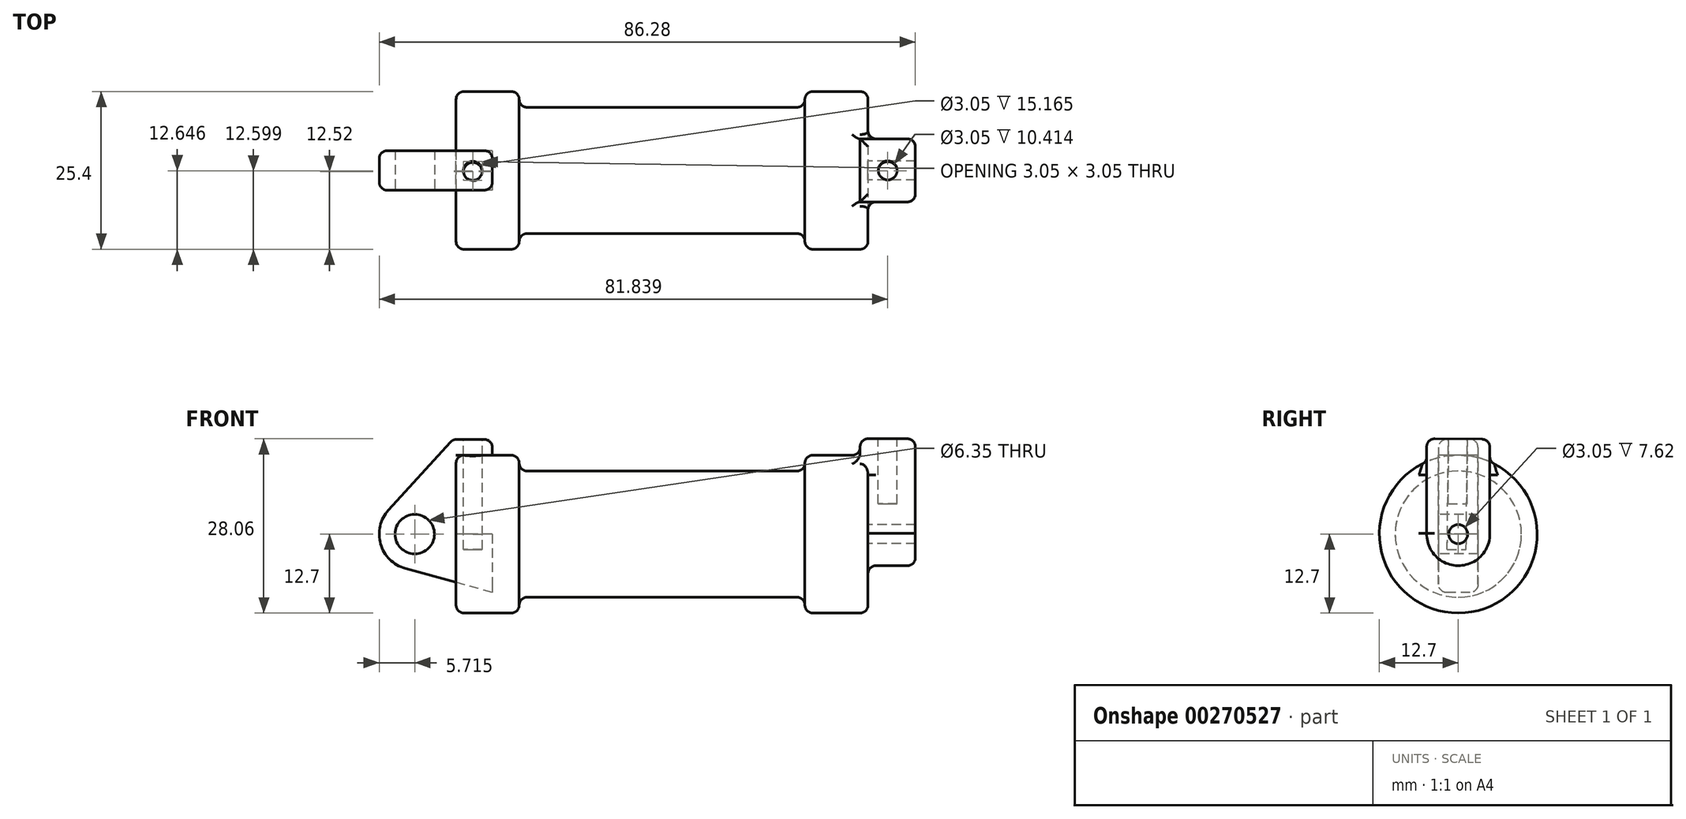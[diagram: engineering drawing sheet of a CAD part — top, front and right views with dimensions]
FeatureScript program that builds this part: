
annotation { "Feature Type Name" : "Feature", "Feature Type Description" : "" }
export const myFeature = defineFeature(function(context is Context, id is Id, definition is map)
    precondition{}
    {
        {
            var Q0;
            Q0=qCreatedBy(makeId("Front.planeOp"),FACE);
            var sketch = newSketch(context, id + "F0", { "sketchPlane" : qUnion([Q0])});
            skLineSegment(sketch, "E0", {"start": v(0, 0) * mm, "end": v(0, 12.7) * mm});
            skLineSegment(sketch, "E1", {"start": v(0, 12.7) * mm, "end": v(10.16, 12.7) * mm});
            skLineSegment(sketch, "E2", {"start": v(10.16, 12.7) * mm, "end": v(10.16, 10.16) * mm});
            skLineSegment(sketch, "E3", {"start": v(10.16, 10.16) * mm, "end": v(56.13, 10.16) * mm});
            skLineSegment(sketch, "E4", {"start": v(56.13, 10.16) * mm, "end": v(56.13, 12.7) * mm});
            skLineSegment(sketch, "E5", {"start": v(56.13, 12.7) * mm, "end": v(66.3, 12.7) * mm});
            skLineSegment(sketch, "E6", {"start": v(66.3, 12.7) * mm, "end": v(66.3, 0) * mm});
            skLineSegment(sketch, "E7", {"start": v(66.3, 0) * mm, "end": v(0, 0) * mm});
            skLineSegment(sketch, "E8", {"start": v(5.84, 15.24) * mm, "end": v(-0.5, 15.24) * mm});
            skLineSegment(sketch, "E9", {"start": v(-0.5, 15.24) * mm, "end": v(-10.88, 3.85) * mm});
            skLineSegment(sketch, "E10", {"start": v(0, 0) * mm, "end": v(-6.65, 0) * mm});
            skCircle(sketch, "E11", {"center": v(-6.65, 0) * mm, "radius": 5.72 * mm});
            skCircle(sketch, "E12", {"center": v(-6.65, 0) * mm, "radius": 3.18 * mm});
            skLineSegment(sketch, "E13", {"start": v(5.84, 15.24) * mm, "end": v(5.84, -9.4) * mm});
            skLineSegment(sketch, "E14", {"start": v(5.84, -9.4) * mm, "end": v(-8.18, -5.5) * mm});
            skSolve(sketch);
        }
        {
            var Q0;
            {var subQ0=sQuery(id+"F0.wireOp",EDGE,"E2");Q0=makeQuery(id+"F0.imprint","IMPRINT",FACE,{"disambiguationData":[TD([[makeQuery(id+"F0.imprint","IMPRINT",EDGE,{"derivedFrom":subQ0}),-1.0]])]});}
            var Q1;
            {var subQ0=sQuery(id+"F0.wireOp",EDGE,"E0");Q1=makeQuery(id+"F0.imprint","IMPRINT",FACE,{"disambiguationData":[TD([[makeQuery(id+"F0.imprint","IMPRINT",EDGE,{"derivedFrom":subQ0}),-1.0]])]});}
            var Q2;
            Q2=sQuery(id+"F0.wireOp",EDGE,"E7");
            revolve(context, id + "F1", {"entities" : qUnion([Q0, Q1]), "axis" : qUnion([Q2]), "revolveType" : RevolveType.FULL});
        }
        {
            var Q0;
            {var subQ3=sQuery(id+"F0.wireOp",EDGE,"E0");Q0=makeQuery(id+"F0.imprint","IMPRINT",FACE,{"disambiguationData":[TD([[makeQuery(id+"F0.imprint","IMPRINT",EDGE,{"derivedFrom":subQ3}),1.0]])]});}
            var Q1;
            {var subQ4=sQuery(id+"F0.wireOp",EDGE,"E12");Q1=makeQuery(id+"F0.imprint","IMPRINT",FACE,{"disambiguationData":[TD([[makeQuery(id+"F0.imprint","IMPRINT",EDGE,{"derivedFrom":subQ4}),-1.0]])]});}
            var Q2;
            {var subQ0=sQuery(id+"F0.wireOp",EDGE,"E14");Q2=makeQuery(id+"F0.imprint","IMPRINT",FACE,{"disambiguationData":[TD([[makeQuery(id+"F0.imprint","IMPRINT",EDGE,{"derivedFrom":subQ0}),-1.0]])]});}
            extrude(context, id + "F2", {"entities" : qUnion([Q0, Q1, Q2]), "endBound" : BoundingType.SYMMETRIC, "oppositeDirection" : true, "depth" : 6.35 * mm});
        }
        {
            var Q0;
            Q0=makeQuery(id+"F1.opRevolve","SWEPT_FACE",FACE,{"disambiguationData":[OSD([sQuery(id+"F0.wireOp",EDGE,"E6")])]});
            var sketch = newSketch(context, id + "F3", { "sketchPlane" : qUnion([Q0])});
            skCircle(sketch, "E15", {"center": v(0, 0) * mm, "radius": 5.08 * mm});
            skCircle(sketch, "E16", {"center": v(0, 0) * mm, "radius": 1.52 * mm});
            skLineSegment(sketch, "E17", {"start": v(5.08, 0.02) * mm, "end": v(5.08, 15.26) * mm});
            skLineSegment(sketch, "E18", {"start": v(-5.08, 0.13) * mm, "end": v(-5.08, 15.37) * mm});
            skLineSegment(sketch, "E19", {"start": v(-5.08, 15.37) * mm, "end": v(5.08, 15.26) * mm});
            skSolve(sketch);
        }
        {
            var Q0;
            Q0 = qSketchRegion(id + "F3", true);
            extrude(context, id + "F4", {"entities" : qUnion([Q0]), "operationType" : NewBodyOperationType.ADD, "depth" : 7.62 * mm, "hasSecondDirection" : true, "secondDirectionOppositeDirection" : true, "secondDirectionDepth" : 1.27 * mm});
        }
        {
            var Q0;
            Q0=makeQuery(id+"F4.opExtrude","SWEPT_FACE",FACE,{"disambiguationData":[OSD([sQuery(id+"F3.wireOp",EDGE,"E19")])]});
            var sketch = newSketch(context, id + "F5", { "sketchPlane" : qUnion([Q0])});
            skCircle(sketch, "E20", {"center": v(69.62, -0.46) * mm, "radius": 1.52 * mm});
            skCircle(sketch, "E21", {"center": v(2.69, -0.23) * mm, "radius": 1.52 * mm});
            skSolve(sketch);
        }
        {
            var Q0;
            Q0=makeQuery(id+"F5.imprint","IMPRINT",FACE,{"disambiguationData":[TD([[makeQuery(id+"F5.imprint","IMPRINT",EDGE,{"derivedFrom":sQuery(id+"F5.wireOp",EDGE,"E21")}),1.0]])]});
            extrude(context, id + "F6", {"entities" : qUnion([Q0]), "operationType" : NewBodyOperationType.REMOVE, "oppositeDirection" : true, "depth" : 17.78 * mm});
        }
        {
            var Q0;
            Q0=makeQuery(id+"F4.opExtrude","SWEPT_FACE",FACE,{"disambiguationData":[OSD([sQuery(id+"F3.wireOp",EDGE,"E19")])]});
            var sketch = newSketch(context, id + "F7", { "sketchPlane" : qUnion([Q0])});
            skCircle(sketch, "E22", {"center": v(69.47, -0.16) * mm, "radius": 1.52 * mm});
            skPoint(sketch, "E22.centerSnap0", {"position": v(69.47, -5.24) * mm});
            skPoint(sketch, "E22.centerSnap1", {"position": v(73.91, -0.16) * mm});
            skSolve(sketch);
        }
        {
            var Q0;
            Q0=makeQuery(id+"F7.imprint","IMPRINT",FACE,{"disambiguationData":[TD([[makeQuery(id+"F7.imprint","IMPRINT",EDGE,{"derivedFrom":sQuery(id+"F7.wireOp",EDGE,"E22")}),1.0]])]});
            extrude(context, id + "F8", {"entities" : qUnion([Q0]), "operationType" : NewBodyOperationType.REMOVE, "oppositeDirection" : true, "depth" : 10.4 * mm});
        }
        {
            var Q0;
            Q0=makeQuery(id+"F1.opRevolve","SWEPT_EDGE",EDGE,{"disambiguationData":[OSD([sQuery(id+"F0.wireOp",EDGE,"E1"),sQuery(id+"F0.wireOp",EDGE,"E2")])]});
            var Q1;
            Q1=makeQuery(id+"F1.opRevolve","SWEPT_EDGE",EDGE,{"disambiguationData":[OSD([sQuery(id+"F0.wireOp",EDGE,"E2"),sQuery(id+"F0.wireOp",EDGE,"E3")])]});
            var Q2;
            Q2=makeQuery(id+"F1.opRevolve","SWEPT_EDGE",EDGE,{"disambiguationData":[OSD([sQuery(id+"F0.wireOp",EDGE,"E0"),sQuery(id+"F0.wireOp",EDGE,"E1")])]});
            var Q3;
            Q3=makeQuery(id+"F1.opRevolve","SWEPT_EDGE",EDGE,{"disambiguationData":[OSD([sQuery(id+"F0.wireOp",EDGE,"E5"),sQuery(id+"F0.wireOp",EDGE,"E6")])]});
            var Q4;
            Q4=makeQuery(id+"F1.opRevolve","SWEPT_EDGE",EDGE,{"disambiguationData":[OSD([sQuery(id+"F0.wireOp",EDGE,"E4"),sQuery(id+"F0.wireOp",EDGE,"E5")])]});
            var Q5;
            Q5=makeQuery(id+"F1.opRevolve","SWEPT_EDGE",EDGE,{"disambiguationData":[OSD([sQuery(id+"F0.wireOp",EDGE,"E3"),sQuery(id+"F0.wireOp",EDGE,"E4")])]});
            fillet(context, id + "F9", {"entities" : qUnion([Q0, Q1, Q2, Q3, Q4, Q5]), "radius" : 1.27 * mm, "tangentPropagation" : true, "allowEdgeOverflow" : false});
        }
        {
            var Q0;
            Q0=makeQuery(id+"F4.opExtrude","CAP_EDGE",EDGE,{"disambiguationData":[OSD([sQuery(id+"F3.wireOp",EDGE,"E18")])],"isStart":false});
            var Q1;
            Q1=makeQuery(id+"F4.opExtrude","SWEPT_EDGE",EDGE,{"disambiguationData":[OSD([sQuery(id+"F3.wireOp",EDGE,"E18"),sQuery(id+"F3.wireOp",EDGE,"E19")])]});
            var Q2;
            Q2=makeQuery(id+"F4.opExtrude","CAP_EDGE",EDGE,{"disambiguationData":[OSD([sQuery(id+"F3.wireOp",EDGE,"E19")])],"isStart":true});
            var Q3;
            Q3=makeQuery(id+"F4.opExtrude","SWEPT_EDGE",EDGE,{"disambiguationData":[OSD([sQuery(id+"F3.wireOp",EDGE,"E17"),sQuery(id+"F3.wireOp",EDGE,"E19")])]});
            var Q4;
            Q4=makeQuery(id+"F4.boolean.opBoolean","INTERSECT",EDGE,{"derivedFrom":[makeQuery(id+"F1.opRevolve","SWEPT_FACE",FACE,{"disambiguationData":[OSD([sQuery(id+"F0.wireOp",EDGE,"E6")])]}),makeQuery(id+"F4.opExtrude","SWEPT_FACE",FACE,{"disambiguationData":[OSD([sQuery(id+"F3.wireOp",EDGE,"E18")])]})]});
            var Q5;
            Q5=makeQuery(id+"F4.opExtrude","CAP_EDGE",EDGE,{"disambiguationData":[OSD([sQuery(id+"F3.wireOp",EDGE,"E15")])],"isStart":false});
            var Q6;
            Q6=makeQuery(id+"F4.boolean.opBoolean","INTERSECT",EDGE,{"derivedFrom":[makeQuery(id+"F1.opRevolve","SWEPT_FACE",FACE,{"disambiguationData":[OSD([sQuery(id+"F0.wireOp",EDGE,"E6")])]}),makeQuery(id+"F4.opExtrude","SWEPT_FACE",FACE,{"disambiguationData":[OSD([sQuery(id+"F3.wireOp",EDGE,"E17")])]})]});
            var Q7;
            Q7=makeQuery(id+"F4.boolean.opBoolean","INTERSECT",EDGE,{"derivedFrom":[makeQuery(id+"F1.opRevolve","SWEPT_FACE",FACE,{"disambiguationData":[OSD([sQuery(id+"F0.wireOp",EDGE,"E5")])]}),makeQuery(id+"F4.opExtrude","CAP_FACE",FACE,{"disambiguationData":[OSD([sQuery(id+"F3.wireOp",EDGE,"E15"),sQuery(id+"F3.wireOp",EDGE,"E16"),sQuery(id+"F3.wireOp",EDGE,"E17"),sQuery(id+"F3.wireOp",EDGE,"E18"),sQuery(id+"F3.wireOp",EDGE,"E19")])],"isStart":true})]});
            var Q8;
            Q8=makeQuery(id+"F4.opExtrude","CAP_EDGE",EDGE,{"disambiguationData":[OSD([sQuery(id+"F3.wireOp",EDGE,"E19")])],"isStart":false});
            fillet(context, id + "F10", {"entities" : qUnion([Q0, Q1, Q2, Q3, Q4, Q5, Q6, Q7, Q8]), "radius" : 1.27 * mm, "tangentPropagation" : true, "allowEdgeOverflow" : false});
        }
        {
            var Q0;
            {var subQ0=sQuery(id+"F0.wireOp",EDGE,"E13");Q0=makeQuery(id+"F2.opExtrude","CAP_EDGE",EDGE,{"disambiguationData":[OSD([subQ0]),TDD([makeQuery(id+"F0.imprint","IMPRINT",EDGE,{"disambiguationData":[TD([[makeQuery(id+"F0.imprint","INTERSECT",VERTEX,{"derivedFrom":[sQuery(id+"F0.wireOp",EDGE,"E8"),subQ0]}),-1.0]])],"derivedFrom":subQ0})])],"isStart":true});}
            var Q1;
            {var subQ0=sQuery(id+"F0.wireOp",EDGE,"E13");Q1=makeQuery(id+"F2.opExtrude","CAP_EDGE",EDGE,{"disambiguationData":[OSD([subQ0]),TDD([makeQuery(id+"F0.imprint","IMPRINT",EDGE,{"disambiguationData":[TD([[makeQuery(id+"F0.imprint","INTERSECT",VERTEX,{"derivedFrom":[sQuery(id+"F0.wireOp",EDGE,"E8"),subQ0]}),-1.0]])],"derivedFrom":subQ0})])],"isStart":false});}
            var Q2;
            Q2=makeQuery(id+"F2.opExtrude","SWEPT_EDGE",EDGE,{"disambiguationData":[OSD([sQuery(id+"F0.wireOp",EDGE,"E8"),sQuery(id+"F0.wireOp",EDGE,"E13")])]});
            var Q3;
            Q3=makeQuery(id+"F2.opExtrude","CAP_EDGE",EDGE,{"disambiguationData":[OSD([sQuery(id+"F0.wireOp",EDGE,"E8")])],"isStart":true});
            var Q4;
            Q4=makeQuery(id+"F2.opExtrude","CAP_EDGE",EDGE,{"disambiguationData":[OSD([sQuery(id+"F0.wireOp",EDGE,"E8")])],"isStart":false});
            var Q5;
            Q5=makeQuery(id+"F2.opExtrude","SWEPT_EDGE",EDGE,{"disambiguationData":[OSD([sQuery(id+"F0.wireOp",EDGE,"E8"),sQuery(id+"F0.wireOp",EDGE,"E9")])]});
            var Q6;
            Q6=makeQuery(id+"F2.opExtrude","CAP_EDGE",EDGE,{"disambiguationData":[OSD([sQuery(id+"F0.wireOp",EDGE,"E9")])],"isStart":true});
            var Q7;
            Q7=makeQuery(id+"F2.opExtrude","CAP_EDGE",EDGE,{"disambiguationData":[OSD([sQuery(id+"F0.wireOp",EDGE,"E11")])],"isStart":true});
            var Q8;
            Q8=makeQuery(id+"F2.opExtrude","CAP_EDGE",EDGE,{"disambiguationData":[OSD([sQuery(id+"F0.wireOp",EDGE,"E14")])],"isStart":true});
            var Q9;
            Q9=makeQuery(id+"F2.opExtrude","CAP_EDGE",EDGE,{"disambiguationData":[OSD([sQuery(id+"F0.wireOp",EDGE,"E14")])],"isStart":false});
            var Q10;
            Q10=makeQuery(id+"F2.opExtrude","CAP_EDGE",EDGE,{"disambiguationData":[OSD([sQuery(id+"F0.wireOp",EDGE,"E11")])],"isStart":false});
            var Q11;
            Q11=makeQuery(id+"F2.opExtrude","CAP_EDGE",EDGE,{"disambiguationData":[OSD([sQuery(id+"F0.wireOp",EDGE,"E9")])],"isStart":false});
            fillet(context, id + "F11", {"entities" : qUnion([Q0, Q1, Q2, Q3, Q4, Q5, Q6, Q7, Q8, Q9, Q10, Q11]), "radius" : 1.27 * mm, "allowEdgeOverflow" : false});
        }
    });
